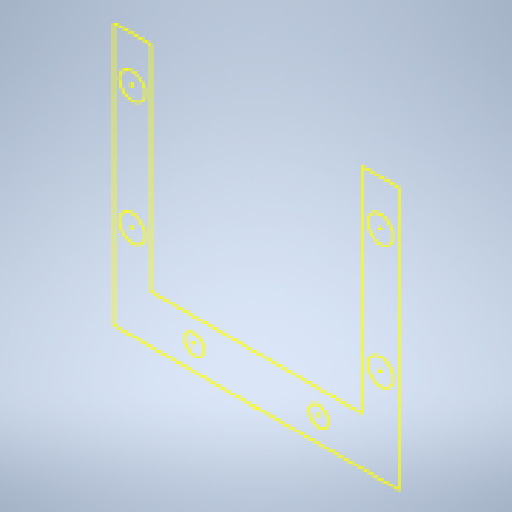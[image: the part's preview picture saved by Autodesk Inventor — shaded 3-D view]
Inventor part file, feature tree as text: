
AUTODESK INVENTOR PART (.ipt)
format: ipt  version: 2023.1 (Build 271208000, 208)  size: 136,192 bytes
history: native  units: mm
features: other x2, extrude x1, sketch x1, reference x1
ambient origin geometry x8: Origin, YZ Plane, XZ Plane, XY Plane, X Axis, Y Axis, Z Axis, Center Point
bodies: Solid1 (feature_tree)
feature tree (5):
  extrude  "Extrusion1"  [1 undecoded]
  sketch  "Sketch1"  dims[d0=49.8mm d1=0.0mm]
  reference  "Reference1"
  other  "Cube 1x1 V5 (Green Laser).iam"
  other  "Cube 1x1 Bottom V5:1"
note: 1 required parameter value undecoded (feature->parameter linkage not recoverable at this tier; creation-order binding heuristic only, values carry confidence <= 0.55)
